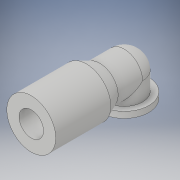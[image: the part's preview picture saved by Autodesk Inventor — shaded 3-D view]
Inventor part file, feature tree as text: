
AUTODESK INVENTOR PART (.ipt)
format: ipt  version: 2018 (Build 220112000, 112)  size: 161,280 bytes
history: native  units: in
note: dims shown in document units (in); Inventor stores cm internally (conversion verified against a paired STEP export)
features: sketch x7, extrude x6, projected_geometry x2, fillet x1, plane x1, loft x1, other x1
ambient origin geometry x8: Origin, YZ Plane, XZ Plane, XY Plane, X Axis, Y Axis, Z Axis, Center Point
bodies: Solid1 (feature_tree)
feature tree (19):
  extrude  "Extrusion1"  Depth=0.05in TaperAngle=0.0deg
  extrude  "Extrusion2"  Depth=0.3in TaperAngle=0.0deg
  extrude  "Extrusion3"  Depth=0.15in
  extrude  "Extrusion4"  Depth=0.2in TaperAngle=0.0deg
  fillet  "Fillet1"  Radius=0.15in
  plane  "Work Plane1"
  loft  "Loft1"
  extrude  "Extrusion5"  Depth=0.15in
  extrude  "Extrusion6"  TaperAngle=0.0deg  [1 undecoded]
  sketch  "Sketch1"  dims[d0=0.4in d1=0.05in d2=0.0in]
  sketch  "Sketch2"  dims[d3=0.3in d4=0.3in d5=0.0in]
  sketch  "Sketch3"  dims[d6=0.3in d7=0.15in]
  sketch  "Sketch4"  dims[d8=0.15in d9=0.2in d10=0.0in d12=0.15in]
  projected_geometry  "Projected Loop1"
  sketch  "Sketch6"  dims[d13=0.15in d14=1.0in d15=0.0in]
  other  "Edges1"
  sketch  "Sketch7"  dims[d16=0.15in d17=0.11in]
  projected_geometry  "Projected Loop3"
  sketch  "Sketch8"  dims[d18=0.4in d19=0.0in d20=90.0deg d21=0.0in d22=90.0deg d23=0.45in d24=0.0in d28=0.1in d29=0.45in d30=0.0in]
note: 1 required parameter value undecoded (feature->parameter linkage not recoverable at this tier; creation-order binding heuristic only, values carry confidence <= 0.55)
